# Revit family: Saxi Varioplan 48T
name_source: partatom
category: Specialty Equipment
revit_build: Autodesk Revit Architecture 2015 (Build: 20140322_1515(x64)
units: mm (PartAtom-declared; Revit-internal decimal feet)

## types (1)
- Saxi Varioplan 48T
    Actual_No_Panels = 5
    Actual_Panel_Width = 691 mm
    CentrumToPanel_Inkörd = 335 mm
    Even_Panels = No
    First_helpanel = 100 mm  [stored 0.328084 ft]
    Height = 2500 mm  [stored 8.2021 ft]
    Karm1 = 100 mm  [stored 0.328084 ft]
    Karm2 = 141 mm
    KarmHeight = 2348 mm
    Manufacturer = Saxi Vägg AB
    Model = Varioplan 48T
    No_Panels = 5
    Panel_Offsets = 691 mm
    Skivbredd = 671 mm
    Skivbredd_Halvpanel = 286 mm
    Skivhöjd = 2278 mm
    TMP1 = 2.5
    TMP2 = 3
    TMP3 = -0.5
    To_Halfpanel = 151 mm  [stored 0.495407 ft]
    URL = http://www.saxi.se
    Wanted_Panel_Width = 700 mm  [stored 2.29659 ft]
    Width = 4000 mm  [stored 13.1234 ft]

note: [stored X ft] marks values corroborated as IEEE doubles in the binary element streams (Revit-internal decimal feet)

## geometry (parser evidence)
native form markers: Sweep x19
no freeform markers — native parametric forms only
